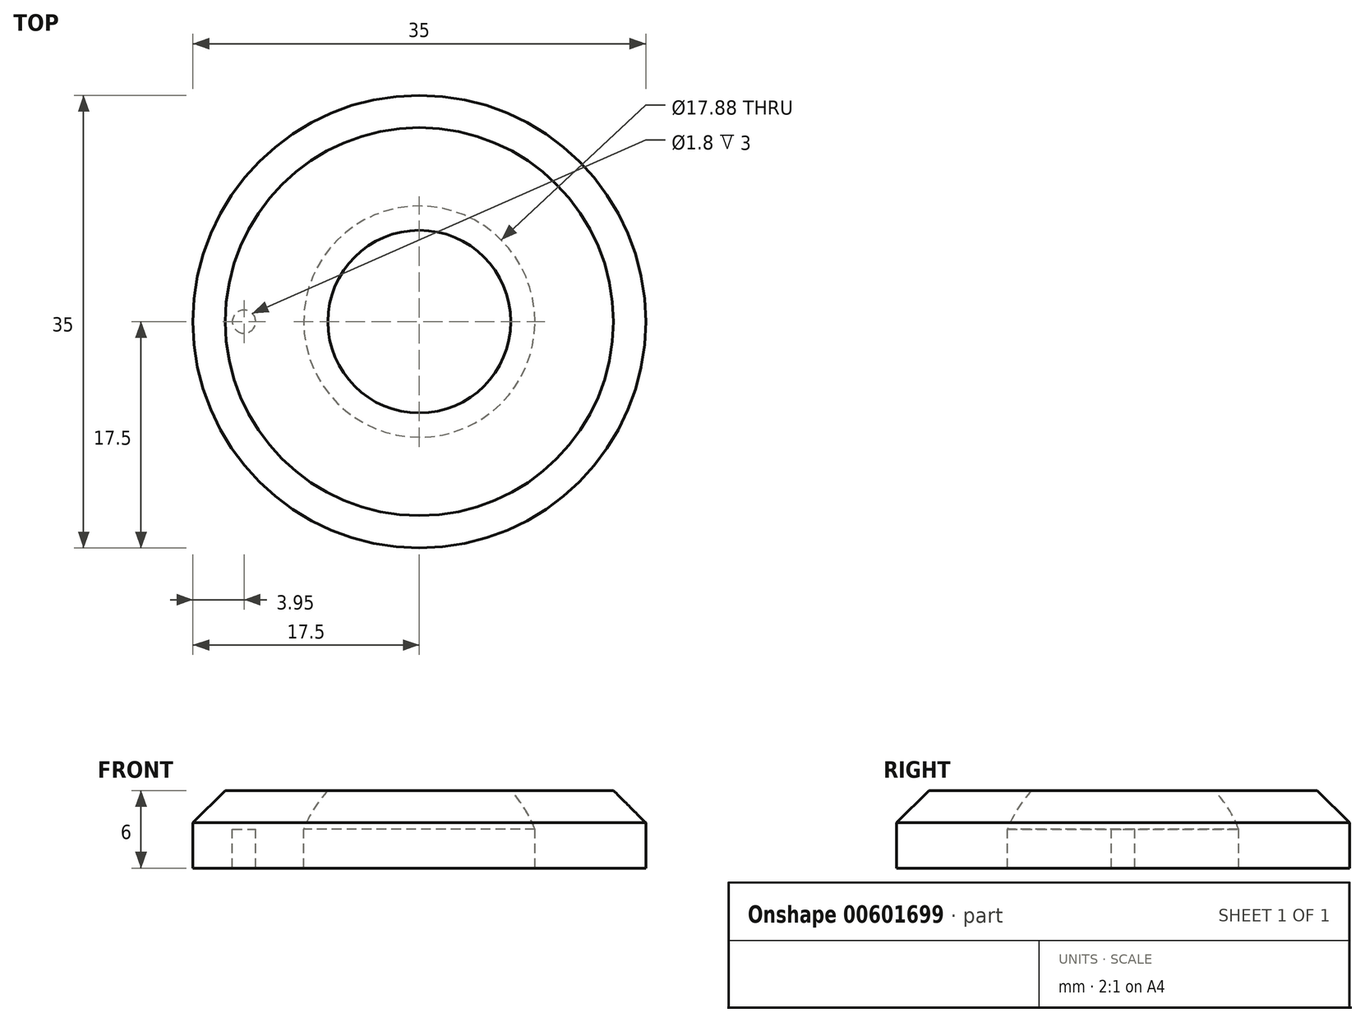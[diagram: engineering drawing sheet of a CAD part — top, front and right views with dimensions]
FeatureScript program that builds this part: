
annotation { "Feature Type Name" : "Feature", "Feature Type Description" : "" }
export const myFeature = defineFeature(function(context is Context, id is Id, definition is map)
    precondition{}
    {
        {
            var Q0;
            Q0=qCreatedBy(makeId("Front.planeOp"),FACE);
            var sketch = newSketch(context, id + "F0", { "sketchPlane" : qUnion([Q0])});
            skLineSegment(sketch, "E0", {"start": v(0, 0) * mm, "end": v(17.5, 0) * mm});
            skLineSegment(sketch, "E1", {"start": v(17.5, 0) * mm, "end": v(17.5, -3) * mm});
            skLineSegment(sketch, "E2", {"start": v(17.5, -3) * mm, "end": v(8.94, -3) * mm});
            skLineSegment(sketch, "E3", {"start": v(0, -3) * mm, "end": v(0, -6.5) * mm, "construction": true});
            skArc(sketch, "E4", {"start": v(8.94, -3) * mm, "mid": v(8.14, -1.41) * mm, "end": v(7.06, 0) * mm});
            skSolve(sketch);
        }
        {
            var Q0;
            Q0 = qSketchRegion(id + "F0", true);
            var Q1;
            Q1=sQuery(id+"F0.wireOp",EDGE,"E3");
            revolve(context, id + "F1", {"entities" : qUnion([Q0]), "axis" : qUnion([Q1]), "revolveType" : RevolveType.FULL});
        }
        {
            var Q0;
            Q0=makeQuery(id+"F1.opRevolve","SWEPT_EDGE",EDGE,{"disambiguationData":[OSD([sQuery(id+"F0.wireOp",EDGE,"E0"),sQuery(id+"F0.wireOp",EDGE,"E1")])]});
            chamfer(context, id + "F2", {"entities" : qUnion([Q0]), "width" : 2.5 * mm, "tangentPropagation" : true});
        }
        {
            var Q0;
            Q0=makeQuery(id+"F1.opRevolve","SWEPT_FACE",FACE,{"disambiguationData":[OSD([sQuery(id+"F0.wireOp",EDGE,"E2")])]});
            var sketch = newSketch(context, id + "F3", { "sketchPlane" : qUnion([Q0])});
            skLineSegment(sketch, "E5", {"start": v(0, 0) * mm, "end": v(13.55, 0) * mm, "construction": true});
            skCircle(sketch, "E6", {"center": v(13.55, 0) * mm, "radius": 0.9 * mm});
            skCircle(sketch, "E7.MirrorC", {"center": v(-13.55, 0) * mm, "radius": 0.9 * mm});
            skSolve(sketch);
        }
        {
            var Q0;
            Q0=makeQuery(id+"F3.imprint","IMPRINT",FACE,{"disambiguationData":[TD([[makeQuery(id+"F3.imprint","IMPRINT",EDGE,{"derivedFrom":sQuery(id+"F3.wireOp",EDGE,"E7.MirrorC")}),-1.0]])]});
            var Q1;
            Q1=makeQuery(id+"F3.imprint","IMPRINT",FACE,{"disambiguationData":[TD([[makeQuery(id+"F3.imprint","IMPRINT",EDGE,{"derivedFrom":sQuery(id+"F3.wireOp",EDGE,"E6")}),1.0]])]});
            extrude(context, id + "F4", {"entities" : qUnion([Q0, Q1]), "operationType" : NewBodyOperationType.ADD, "depth" : 3 * mm, "offsetDistance" : 25 * mm});
        }
    });
